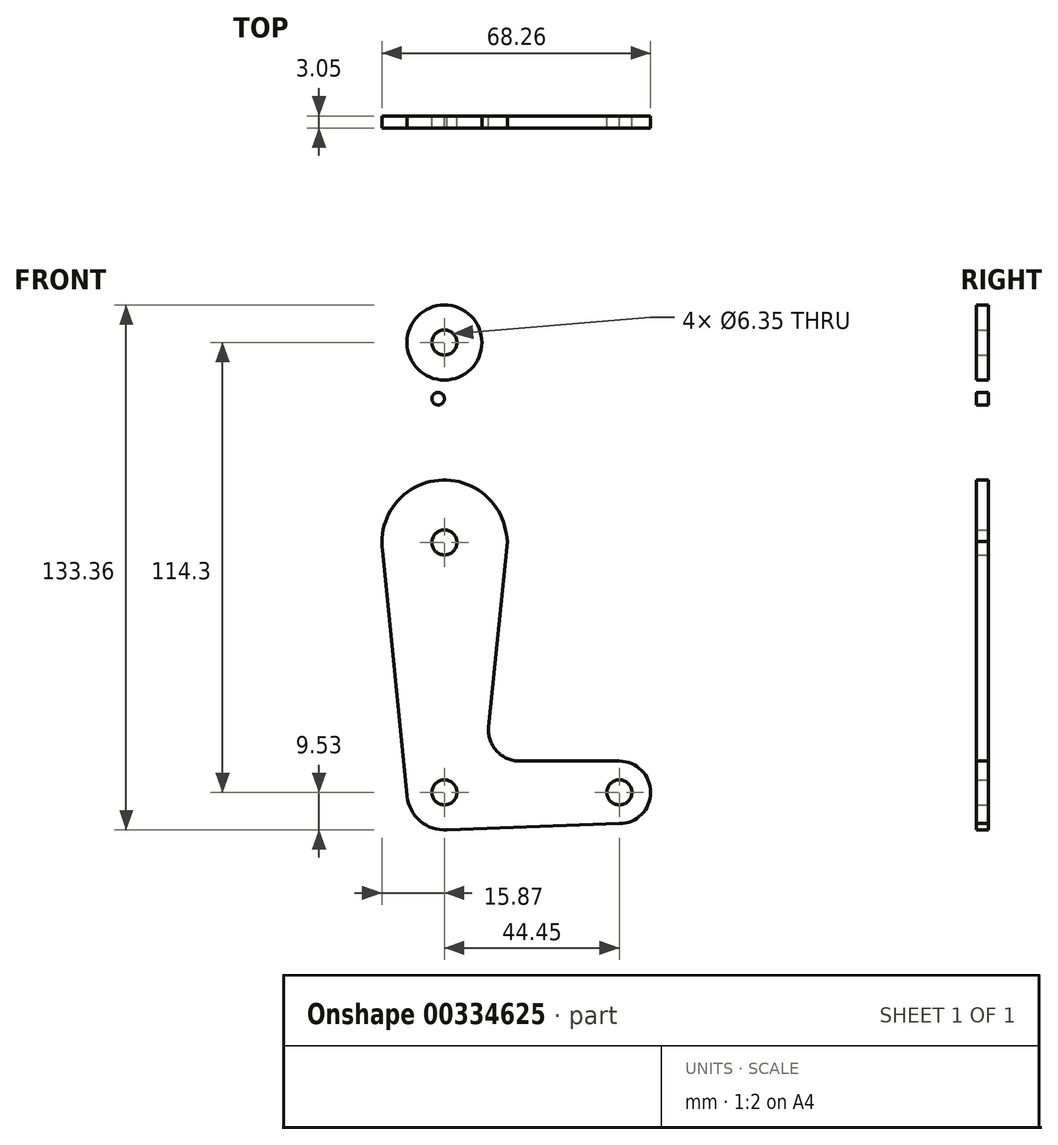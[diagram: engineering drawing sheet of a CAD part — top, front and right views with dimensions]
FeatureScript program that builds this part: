
annotation { "Feature Type Name" : "Feature", "Feature Type Description" : "" }
export const myFeature = defineFeature(function(context is Context, id is Id, definition is map)
    precondition{}
    {
        {
            var Q0;
            Q0=qCreatedBy(makeId("Front.planeOp"),FACE);
            var sketch = newSketch(context, id + "F0", { "sketchPlane" : qUnion([Q0])});
            skLineSegment(sketch, "E0", {"start": v(0, 0) * mm, "end": v(44.45, 0) * mm, "construction": true});
            skLineSegment(sketch, "E1", {"start": v(0, 0) * mm, "end": v(0, 114.3) * mm, "construction": true});
            skCircle(sketch, "E2", {"center": v(0, 0) * mm, "radius": 9.53 * mm});
            skCircle(sketch, "E3", {"center": v(44.45, 0) * mm, "radius": 7.94 * mm});
            skCircle(sketch, "E4", {"center": v(0, 114.3) * mm, "radius": 9.53 * mm});
            skCircle(sketch, "E5", {"center": v(0, 63.5) * mm, "radius": 15.88 * mm});
            skLineSegment(sketch, "E6", {"start": v(9.53, 114.3) * mm, "end": v(15.98, 63.71) * mm});
            skLineSegment(sketch, "E7", {"start": v(15.98, 63.71) * mm, "end": v(11.25, 16.68) * mm});
            skLineSegment(sketch, "E8", {"start": v(19.16, 7.94) * mm, "end": v(44.45, 7.94) * mm});
            skLineSegment(sketch, "E9", {"start": v(0, -9.52) * mm, "end": v(44.45, -7.94) * mm});
            skCircle(sketch, "E10", {"center": v(0, 114.3) * mm, "radius": 3.18 * mm});
            skCircle(sketch, "E11", {"center": v(0, 63.5) * mm, "radius": 3.18 * mm});
            skCircle(sketch, "E12", {"center": v(0, 0) * mm, "radius": 3.18 * mm});
            skCircle(sketch, "E13", {"center": v(44.45, 0) * mm, "radius": 3.18 * mm});
            skCircle(sketch, "E14", {"center": v(-1.59, 100.03) * mm, "radius": 1.59 * mm});
            skArc(sketch, "E15.filletArc", {"start": v(11.25, 16.68) * mm, "mid": v(13.26, 10.55) * mm, "end": v(19.16, 7.94) * mm});
            skLineSegment(sketch, "E16", {"start": v(-15.88, 63.5) * mm, "end": v(-9.48, -0.94) * mm});
            skLineSegment(sketch, "E17", {"start": v(-9.52, 114.3) * mm, "end": v(-18.32, 66.65) * mm});
            skSolve(sketch);
        }
        {
            var Q0;
            Q0 = qSketchRegion(id + "F0", true);
            extrude(context, id + "F1", {"entities" : qUnion([Q0]), "depth" : 3.05 * mm});
        }
    });
